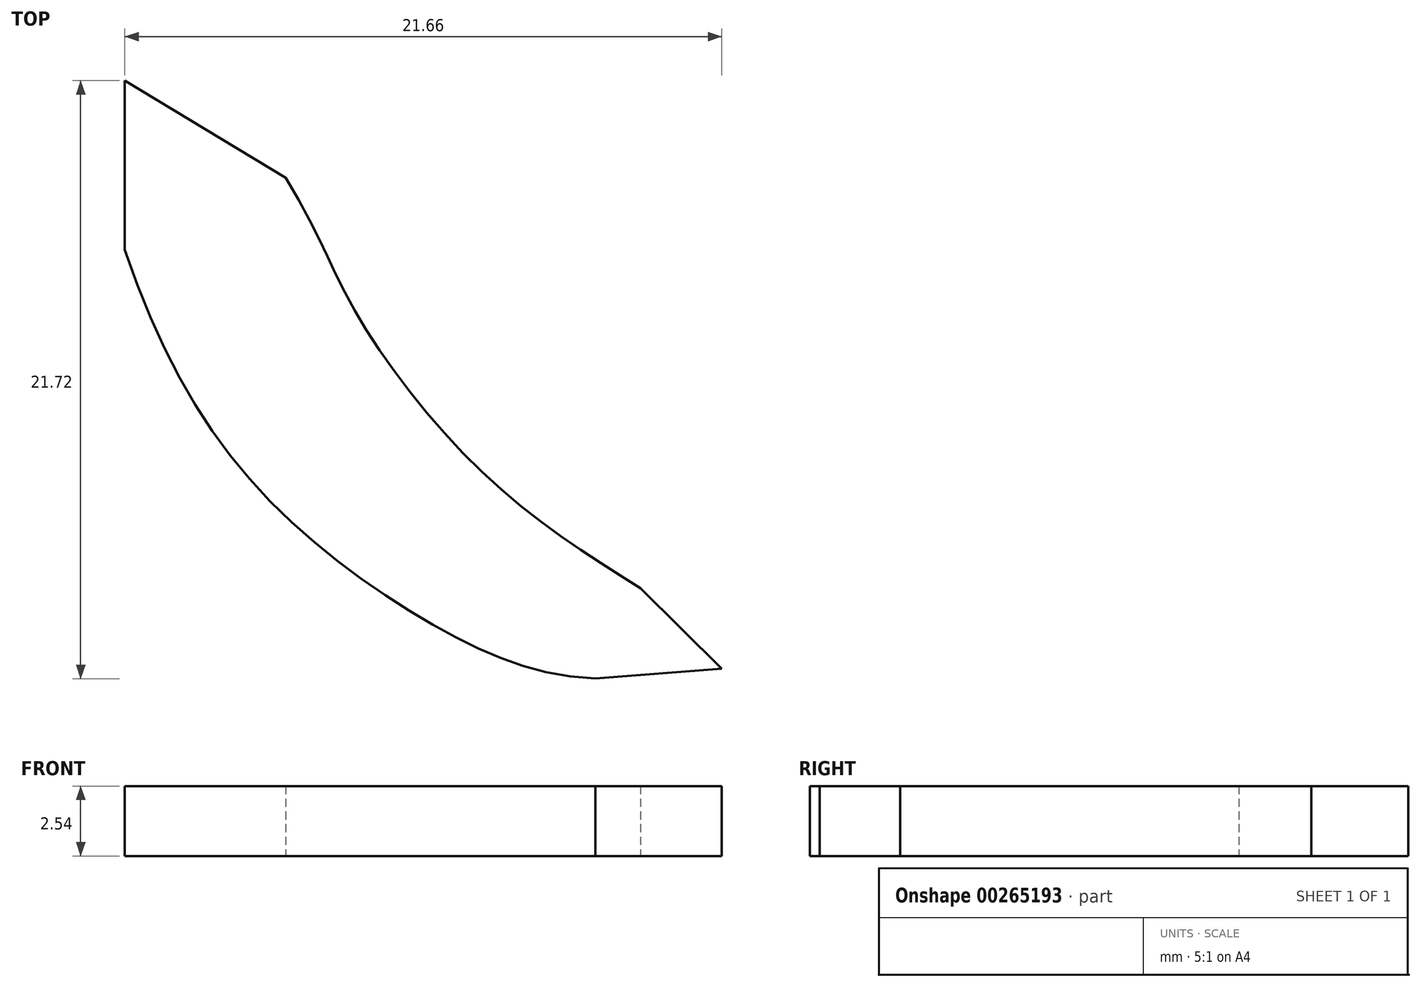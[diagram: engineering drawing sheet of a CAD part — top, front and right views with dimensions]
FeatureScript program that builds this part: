
annotation { "Feature Type Name" : "Feature", "Feature Type Description" : "" }
export const myFeature = defineFeature(function(context is Context, id is Id, definition is map)
    precondition{}
    {
        {
            var Q0;
            Q0=qCreatedBy(makeId("Top.planeOp"),FACE);
            var sketch = newSketch(context, id + "F0", { "sketchPlane" : qUnion([Q0])});
            skLineSegment(sketch, "E0.bottom", {"start": v(-12.7, 12.7) * mm, "end": v(12.7, 12.7) * mm, "construction": true});
            skLineSegment(sketch, "E0.top", {"start": v(-12.7, -12.7) * mm, "end": v(12.7, -12.7) * mm, "construction": true});
            skLineSegment(sketch, "E0.left", {"start": v(-12.7, 12.7) * mm, "end": v(-12.7, -12.7) * mm, "construction": true});
            skLineSegment(sketch, "E0.right", {"start": v(12.7, 12.7) * mm, "end": v(12.7, -12.7) * mm, "construction": true});
            skPoint(sketch, "E0.middle", {"position": v(0, 0) * mm});
            skLineSegment(sketch, "E1", {"start": v(-12.7, 12.7) * mm, "end": v(-12.7, 6.55) * mm});
            skFitSpline(sketch, "E2", {"points": [v(-12.7, 6.55) * mm, v(-7.68, -2.31) * mm, v(-1.14, -7.27) * mm, v(4.37, -9.02) * mm], "startDerivative": vector(10.13, -30.08) * mm, "endDerivative": vector(21.7, -1) * mm});
            skFitSpline(sketch, "E3", {"points": [v(-6.87, 9.18) * mm, v(-4.4, 4.44) * mm, v(0.33, -1.58) * mm, v(6.01, -5.74) * mm], "startDerivative": vector(12.13, -19.43) * mm, "endDerivative": vector(16.35, -10.27) * mm});
            skLineSegment(sketch, "E4", {"start": v(6.01, -5.74) * mm, "end": v(8.96, -8.66) * mm});
            skLineSegment(sketch, "E5", {"start": v(8.96, -8.66) * mm, "end": v(4.37, -9.02) * mm});
            skLineSegment(sketch, "E6", {"start": v(-12.7, 12.7) * mm, "end": v(-6.87, 9.18) * mm});
            skSolve(sketch);
        }
        {
            var Q0;
            Q0 = qSketchRegion(id + "F0", true);
            extrude(context, id + "F1", {"entities" : qUnion([Q0]), "depth" : 2.54 * mm});
        }
    });
